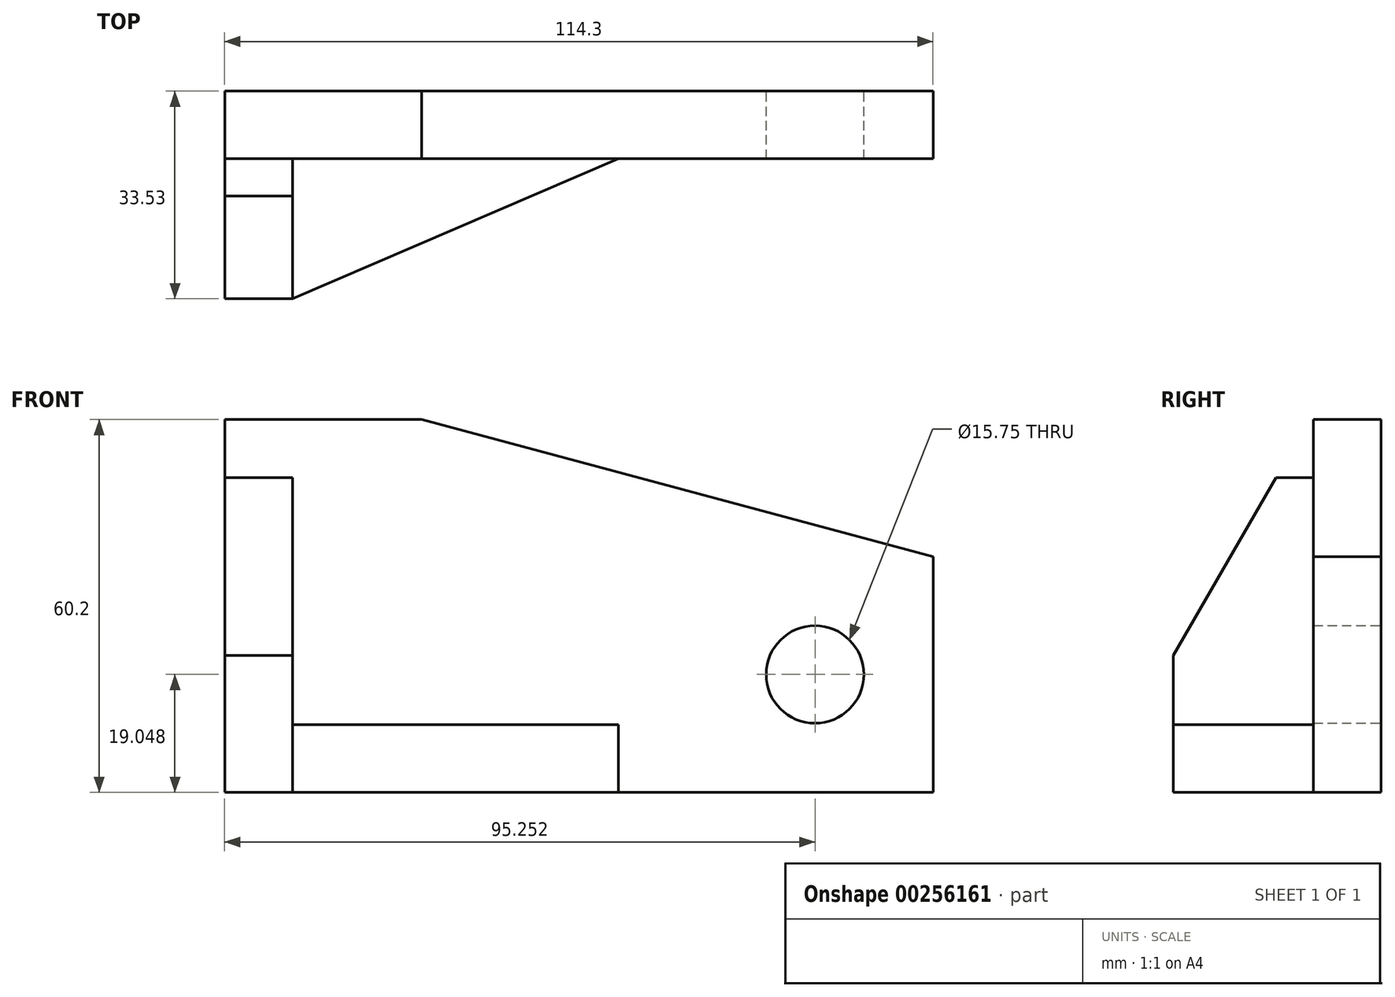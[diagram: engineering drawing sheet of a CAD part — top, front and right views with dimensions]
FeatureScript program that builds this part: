
annotation { "Feature Type Name" : "Feature", "Feature Type Description" : "" }
export const myFeature = defineFeature(function(context is Context, id is Id, definition is map)
    precondition{}
    {
        {
            var Q0;
            Q0=qCreatedBy(makeId("Front.planeOp"),FACE);
            var sketch = newSketch(context, id + "F0", { "sketchPlane" : qUnion([Q0])});
            skLineSegment(sketch, "E0", {"start": v(-45.98, 3.34) * mm, "end": v(-14.23, 3.34) * mm});
            skLineSegment(sketch, "E1", {"start": v(-14.23, 3.34) * mm, "end": v(68.32, -18.78) * mm});
            skLineSegment(sketch, "E2", {"start": v(68.32, -18.78) * mm, "end": v(68.32, -56.86) * mm});
            skLineSegment(sketch, "E3", {"start": v(68.32, -56.86) * mm, "end": v(-45.98, -56.86) * mm});
            skLineSegment(sketch, "E4", {"start": v(-45.98, 3.34) * mm, "end": v(-45.98, -56.86) * mm});
            skLineSegment(sketch, "E5", {"start": v(-45.98, -6.06) * mm, "end": v(-35.06, -6.06) * mm});
            skLineSegment(sketch, "E6", {"start": v(-35.06, -6.06) * mm, "end": v(-35.06, -45.94) * mm});
            skLineSegment(sketch, "E7", {"start": v(-35.06, -45.94) * mm, "end": v(17.52, -45.94) * mm});
            skLineSegment(sketch, "E8", {"start": v(17.52, -45.94) * mm, "end": v(17.52, -56.86) * mm});
            skCircle(sketch, "E9", {"center": v(49.27, -37.81) * mm, "radius": 7.87 * mm});
            skLineSegment(sketch, "E10", {"start": v(49.27, -31.58) * mm, "end": v(49.27, -56.86) * mm, "construction": true});
            skLineSegment(sketch, "E11", {"start": v(41.2, -37.81) * mm, "end": v(68.32, -37.81) * mm, "construction": true});
            skSolve(sketch);
        }
        {
            var Q0;
            Q0 = qSketchRegion(id + "F0", true);
            extrude(context, id + "F1", {"entities" : qUnion([Q0]), "depth" : 10.92 * mm});
        }
        {
            var Q0;
            {var subQ0=sQuery(id+"F0.wireOp",EDGE,"E5");Q0=makeQuery(id+"F0.imprint","IMPRINT",FACE,{"disambiguationData":[TD([[makeQuery(id+"F0.imprint","IMPRINT",EDGE,{"derivedFrom":subQ0}),-1.0]])]});}
            extrude(context, id + "F2", {"entities" : qUnion([Q0]), "operationType" : NewBodyOperationType.ADD, "depth" : 33.53 * mm});
        }
        {
            var Q0;
            Q0=makeQuery(id+"F2.opExtrude","SWEPT_FACE",FACE,{"disambiguationData":[OSD([sQuery(id+"F0.wireOp",EDGE,"E7")])]});
            var sketch = newSketch(context, id + "F3", { "sketchPlane" : qUnion([Q0])});
            skLineSegment(sketch, "E12", {"start": v(-35.06, -33.53) * mm, "end": v(17.52, -10.92) * mm});
            skSolve(sketch);
        }
        {
            var Q0;
            Q0=makeQuery(id+"F3.imprint","IMPRINT",FACE,{"disambiguationData":[TD([[makeQuery(id+"F3.imprint","IMPRINT",EDGE,{"derivedFrom":sQuery(id+"F3.wireOp",EDGE,"E12")}),-1.0]])]});
            extrude(context, id + "F4", {"entities" : qUnion([Q0]), "operationType" : NewBodyOperationType.REMOVE, "endBound" : BoundingType.THROUGH_ALL, "oppositeDirection" : true, "depth" : 25.4 * mm});
        }
        {
            var Q0;
            Q0=makeQuery(id+"F2.opExtrude","CAP_EDGE",EDGE,{"disambiguationData":[OSD([sQuery(id+"F0.wireOp",EDGE,"E5")])],"isStart":false});
            chamfer(context, id + "F5", {"entities" : qUnion([Q0]), "chamferType" : ChamferType.OFFSET_ANGLE, "width" : 28.7 * mm, "oppositeDirection" : true, "angle" : 30 * degree, "tangentPropagation" : true});
        }
    });
